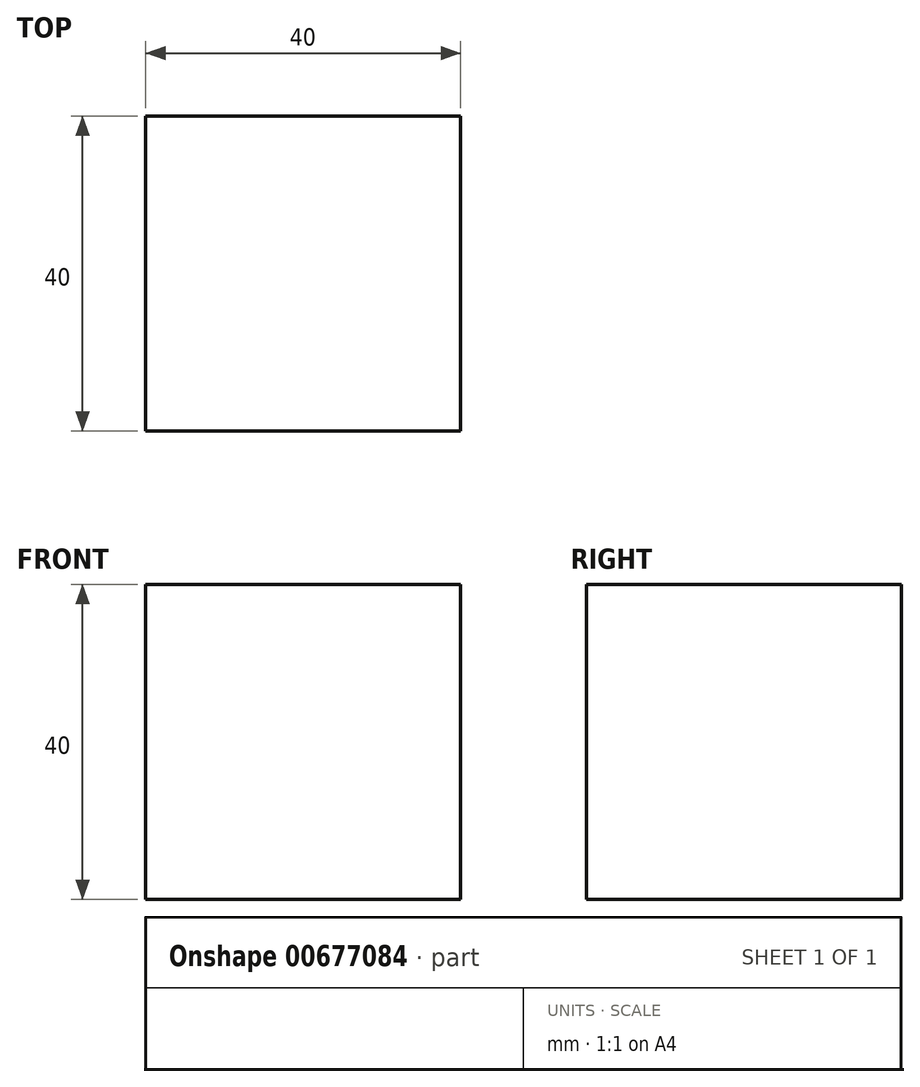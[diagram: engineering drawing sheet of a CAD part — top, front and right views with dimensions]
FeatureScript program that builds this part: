
annotation { "Feature Type Name" : "Feature", "Feature Type Description" : "" }
export const myFeature = defineFeature(function(context is Context, id is Id, definition is map)
    precondition{}
    {
        {
            var Q0;
            Q0=qCreatedBy(makeId("Top.planeOp"),FACE);
            var sketch = newSketch(context, id + "F0", { "sketchPlane" : qUnion([Q0])});
            skLineSegment(sketch, "E0.bottom", {"start": v(-20, 20) * mm, "end": v(20, 20) * mm});
            skLineSegment(sketch, "E0.top", {"start": v(-20, -20) * mm, "end": v(20, -20) * mm});
            skLineSegment(sketch, "E0.left", {"start": v(-20, 20) * mm, "end": v(-20, -20) * mm});
            skLineSegment(sketch, "E0.right", {"start": v(20, 20) * mm, "end": v(20, -20) * mm});
            skPoint(sketch, "E0.middle", {"position": v(0, 0) * mm});
            skSolve(sketch);
        }
        {
            var Q0;
            Q0=makeQuery(id+"F0.imprint","IMPRINT",FACE,{"disambiguationData":[TD([[makeQuery(id+"F0.imprint","IMPRINT",EDGE,{"derivedFrom":sQuery(id+"F0.wireOp",EDGE,"E0.bottom")}),-1.0]])]});
            extrude(context, id + "F1", {"entities" : qUnion([Q0]), "depth" : 40 * mm, "offsetDistance" : 25 * mm});
        }
    });
